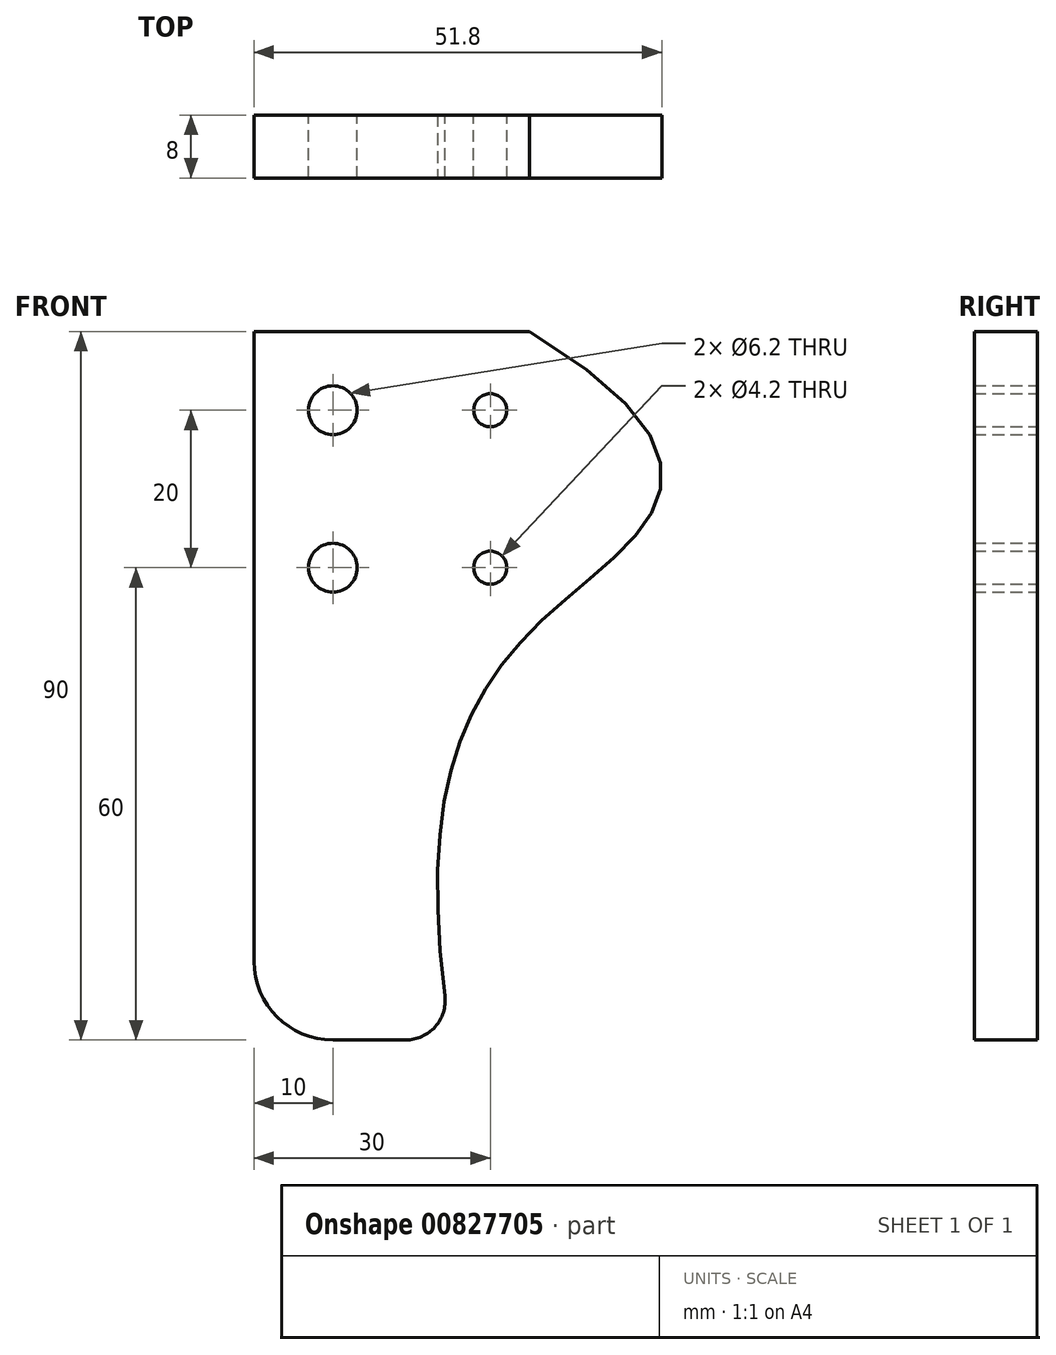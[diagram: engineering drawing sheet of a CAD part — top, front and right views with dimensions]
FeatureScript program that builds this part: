
annotation { "Feature Type Name" : "Feature", "Feature Type Description" : "" }
export const myFeature = defineFeature(function(context is Context, id is Id, definition is map)
    precondition{}
    {
        {
            var Q0;
            Q0=qCreatedBy(makeId("Front.planeOp"),FACE);
            var sketch = newSketch(context, id + "F0", { "sketchPlane" : qUnion([Q0])});
            skLineSegment(sketch, "E0.left", {"start": v(-150, 40) * mm, "end": v(-150, -50) * mm});
            skPoint(sketch, "E0.middle", {"position": v(0, 0) * mm});
            skCircle(sketch, "E1", {"center": v(-140, 30) * mm, "radius": 3.1 * mm});
            skCircle(sketch, "E2", {"center": v(-140, 10) * mm, "radius": 3.1 * mm});
            skLineSegment(sketch, "E3", {"start": v(-150, -50) * mm, "end": v(-125, -50) * mm});
            skLineSegment(sketch, "E4", {"start": v(-150, 40) * mm, "end": v(-115, 40) * mm});
            skFitSpline(sketch, "E5", {"points": [v(-125, -50) * mm, v(-112.45, 4.25) * mm, v(-115, 40) * mm], "startDerivative": vector(-23.28, 151.65) * mm, "endDerivative": vector(-200.24, 121.42) * mm});
            skCircle(sketch, "E6", {"center": v(-120, 30) * mm, "radius": 2.1 * mm});
            skCircle(sketch, "E7", {"center": v(-120, 10) * mm, "radius": 2.1 * mm});
            skSolve(sketch);
        }
        {
            assignVariable(context, id + "F1", {"name" : "Plexiglas", "anyValue" : 8});
        }
        {
            var Q0;
            Q0=makeQuery(id+"F0.imprint","IMPRINT",FACE,{"disambiguationData":[TD([[makeQuery(id+"F0.imprint","IMPRINT",EDGE,{"derivedFrom":sQuery(id+"F0.wireOp",EDGE,"E0.left")}),1.0]])]});
            extrude(context, id + "F2", {"entities" : qUnion([Q0]), "depth" : (getVariable(context, 'Plexiglas')) * mm, "offsetDistance" : 25 * mm});
        }
        {
            var Q0;
            Q0=makeQuery(id+"F2.opExtrude","SWEPT_EDGE",EDGE,{"disambiguationData":[OSD([sQuery(id+"F0.wireOp",EDGE,"E0.left"),sQuery(id+"F0.wireOp",EDGE,"E3")])]});
            fillet(context, id + "F3", {"entities" : qUnion([Q0]), "radius" : 10 * mm, "tangentPropagation" : true, "allowEdgeOverflow" : false});
        }
        {
            var Q0;
            Q0=makeQuery(id+"F2.opExtrude","SWEPT_EDGE",EDGE,{"disambiguationData":[OSD([sQuery(id+"F0.wireOp",EDGE,"E3"),sQuery(id+"F0.wireOp",EDGE,"E5")])]});
            fillet(context, id + "F4", {"entities" : qUnion([Q0]), "radius" : 5 * mm, "tangentPropagation" : true, "allowEdgeOverflow" : false});
        }
    });
